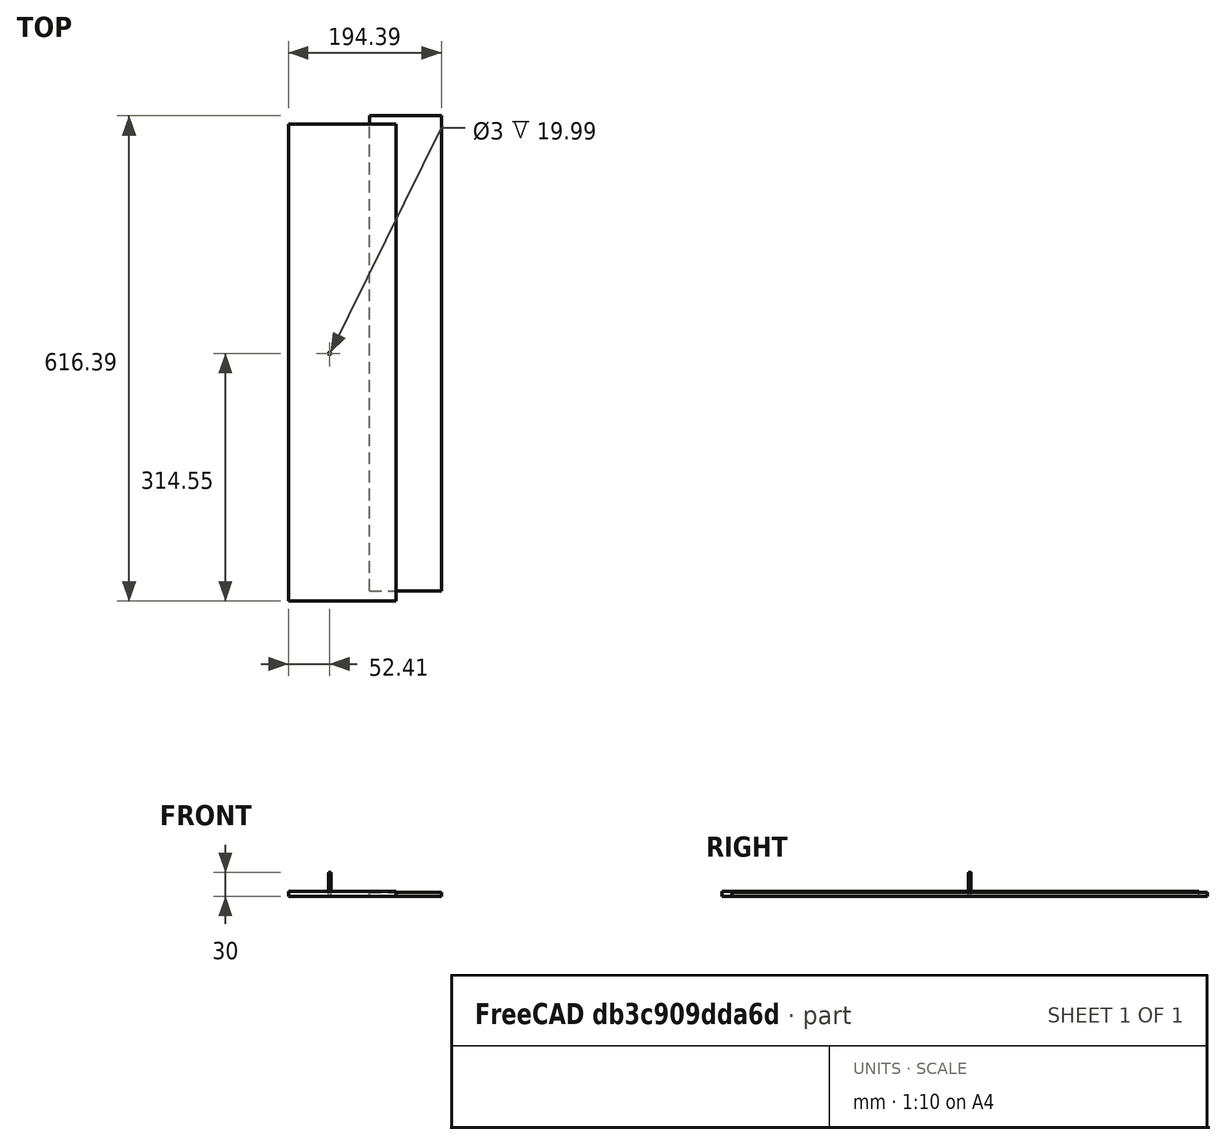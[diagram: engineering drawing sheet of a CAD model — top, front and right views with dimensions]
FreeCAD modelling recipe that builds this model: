
FCSTD DOCUMENT  (FreeCAD 0.22R34651 (Git))
Label: composit_stand7_PP_cut
License: All rights reserved
LicenseURL: http://en.wikipedia.org/wiki/All_rights_reserved
objects: App::DocumentObjectGroup×7, Part::FeaturePython×6, Path::FeaturePython×5, Part::Part2DObjectPython×4, App::FeaturePython×1, App::Link×1, Path::FeatureCompound×1
note: 14 computed .brp shape members not serialized (recipe doc carries the construction recipe); baked Part::Feature solids carry a one-line shape summary decoded from their .brp
EXTERNAL_REF file=composit_stand7.FCStd obj=Body003

FEATURE [App::DocumentObjectGroup] Group003  label="sink2_Group"
FEATURE [App::DocumentObjectGroup] Group001  label="unfolds"
  Group = -> [Group003]
FEATURE [App::FeaturePython] SetupSheet  # Path/CAM operation (typed FeaturePython)
  ClearanceHeightExpression = OpStockZMax+SetupSheet.ClearanceHeightOffset
  ClearanceHeightOffset = 5
  CoolantMode = 0
  CoolantModes = None | Flood | Mist
  FinalDepthExpression = -0.1 mm
  HorizRapid = 0
  ProfileDirection = 1
  ProfileSide = 0
  ProfileUseComp = true
  ProfileprocessCircles = true
  ProfileprocessHoles = true
  ProfileprocessPerimeter = true
  SafeHeightExpression = OpStockZMax+SetupSheet.SafeHeightOffset
  SafeHeightOffset = 3
  StartDepthExpression = 3 mm
  StepDownExpression = 4 mm
  VertRapid = 0
FEATURE [Part::FeaturePython] ToolBit  label="3.175mm Endmill"  # Path/CAM toolbit (typed FeaturePython)
  BitPropertyNames = Chipload | CuttingEdgeHeight | Diameter | Flutes | Length | Material | ShankDiameter | SpindleDirection
  BitShape = <path>
  Chipload = 0
  CuttingEdgeHeight = 30
  Diameter = 3.17
  Flutes = 0
  Length = 10
  Material = 0
  ShankDiameter = 3
  ShapeName = endmill
  SpindleDirection = 0
FEATURE [Path::FeaturePython] __175mm_Endmill  label="3.175mm Endmill001"  # Path/CAM operation (typed FeaturePython)
  HorizFeed = 33.3333
  HorizRapid = 0
  SpindleDir = 0
  SpindleSpeed = 18000
  Tool = -> ToolBit
  ToolNumber = 1
  VertFeed = 35
  VertRapid = 0
  expr: HorizRapid = SetupSheet.HorizRapid
  expr: VertRapid = SetupSheet.VertRapid
FEATURE [App::DocumentObjectGroup] Tools
  Group = -> [__175mm_Endmill]
FEATURE [Part::Part2DObjectPython] Rectangle  # Draft 2D object (typed FeaturePython)
  Area = 0
  ChamferSize = 0
  Columns = 1
  FilletRadius = 0
  Height = 1500
  Length = 1500
  MakeFace = false
  Rows = 1
FEATURE [App::Link] Link  label="top_dropper_fix"
  LinkedObject = -> <external composit_stand7.FCStd>#Body003
FEATURE [App::DocumentObjectGroup] Group  label="parts"
  Group = -> [Link]
FEATURE [Part::FeaturePython] Clone  label="Model-top_dropper_fix"  # Draft clone (typed FeaturePython)
  AttacherType = Attacher::AttachEngine3D
  Fuse = false
  Objects = -> [Link]
  PathResource = Model
  Placement = pos=(38.9812,0,5) rot=(0.707107,0.707107,0;3.14159rad)
  Scale = (1,1,1)
FEATURE [Part::FeaturePython] Clone001  label="Model-top_dropper_fix001"  # Draft clone (typed FeaturePython)
  AttacherType = Attacher::AttachEngine3D
  Fuse = false
  Objects = -> [Link]
  PathResource = Model
  Placement = pos=(82.6289,0,5) rot=(0.707107,0.707107,0;3.14159rad)
  Scale = (1,1,1)
FEATURE [App::DocumentObjectGroup] Model
  Group = -> [Clone,Clone001]
FEATURE [Part::FeaturePython] Stock  # WARN: FeaturePython — macro-defined, semantics opaque (R4)
  Base = -> Model
  ExtXneg = 1
  ExtXpos = 1
  ExtYneg = 1
  ExtYpos = 1
  ExtZneg = 0
  ExtZpos = 1
  Placement = pos=(-51.4071,-313.554,-1.68e-13) rot=(0,0,1;0rad)
  StockType = FromBase
FEATURE [Path::FeaturePython] Profile  # Path/CAM operation (typed FeaturePython)
  Active = false
  AreaParams:
    Tolerance = 1e-07
    FitArcs = True
    Simplify = False
    CleanDistance = 0.0
    Accuracy = 0.01
    Unit = 1.0
    MinArcPoints = 4
    MaxArcPoints = 100
    ClipperScale = 10000000.0
    Fill = 0
    Coplanar = 0
    Reorient = True
    Outline = False
    Explode = False
    OpenMode = 0
    Deflection = 0.01
    SubjectFill = 0
    ClipFill = 0
    Offset = -1.585
    ExtraPass = 0
    Stepover = 0.0
    LastStepover = 0.0
    JoinType = 0
    EndType = 0
    MiterLimit = 2.0
    RoundPrecision = 0.0
    PocketMode = 0
    ToolRadius = 1.0
    PocketExtraOffset = 0.0
    PocketStepover = 0.0
    PocketLastStepover = 0.0
    FromCenter = False
    Angle = 45.0
    AngleShift = 0.0
    Shift = 0.0
    Thicken = False
    SectionCount = -1
    Stepdown = 1.0
    SectionOffset = 0.0
    SectionTolerance = 1e-07
    SectionMode = 2
    Project = False
  Base = -> [Clone,Clone001]
  ClearanceHeight = 11
  CoolantMode = 0
  CycleTime = 00:01:07
  Direction = 1
  FinalDepth = -0.1
  HandleMultipleFeatures = 0
  JoinType = 0
  MiterLimit = 0.1
  OffsetExtra = 0
  OpFinalDepth = -1.68e-13
  OpStartDepth = 6
  OpStockZMax = 6
  OpStockZMin = -1.68e-13
  OpToolDiameter = 3.17
  PathParams = {'orientation': 1, 'feedrate': 33.333333333333336, 'feedrate_v': 35.0, 'verbose': True, 'resume_height': 8.999999999999858, 'retraction': 10.999999999999858, 'return_end': True, 'preamble': False, 'start': Vector (166.08630580869018, 278.409351642555, 10.999999999999858)}
  SafeHeight = 9
  Side = 0
  SplitArcs = false
  StartDepth = 3
  StartPoint = (0,0,0)
  StepDown = 4
  ToolController = -> __175mm_Endmill
  UseComp = true
  UseStartPoint = false
  processCircles = true
  processHoles = true
  processPerimeter = false
  expr: ClearanceHeight = OpStockZMax + SetupSheet.ClearanceHeightOffset
  expr: FinalDepth = -0.1 mm
  expr: SafeHeight = OpStockZMax + SetupSheet.SafeHeightOffset
  expr: StartDepth = 3 mm
  expr: StepDown = 4 mm
FEATURE [Path::FeaturePython] Profile001  # Path/CAM operation (typed FeaturePython)
  Active = true
  AreaParams:
    Tolerance = 1e-07
    FitArcs = True
    Simplify = False
    CleanDistance = 0.0
    Accuracy = 0.01
    Unit = 1.0
    MinArcPoints = 4
    MaxArcPoints = 100
    ClipperScale = 10000000.0
    Fill = 0
    Coplanar = 0
    Reorient = True
    Outline = False
    Explode = False
    OpenMode = 0
    Deflection = 0.01
    SubjectFill = 0
    ClipFill = 0
    Offset = 1.585
    ExtraPass = 0
    Stepover = 0.0
    LastStepover = 0.0
    JoinType = 0
    EndType = 0
    MiterLimit = 2.0
    RoundPrecision = 0.0
    PocketMode = 0
    ToolRadius = 1.0
    PocketExtraOffset = 0.0
    PocketStepover = 0.0
    PocketLastStepover = 0.0
    FromCenter = False
    Angle = 45.0
    AngleShift = 0.0
    Shift = 0.0
    Thicken = False
    SectionCount = -1
    Stepdown = 1.0
    SectionOffset = 0.0
    SectionTolerance = 1e-07
    SectionMode = 2
    Project = False
  Base = -> [Clone,Clone001]
  ClearanceHeight = 11
  CoolantMode = 0
  CycleTime = 00:01:29
  Direction = 1
  FinalDepth = -0.1
  HandleMultipleFeatures = 0
  JoinType = 0
  MiterLimit = 0.1
  OffsetExtra = 0
  OpFinalDepth = -1.68e-13
  OpStartDepth = 6
  OpStockZMax = 6
  OpStockZMin = -1.68e-13
  OpToolDiameter = 3.17
  PathParams = {'orientation': 0, 'feedrate': 33.333333333333336, 'feedrate_v': 35.0, 'verbose': True, 'resume_height': 8.999999999999858, 'retraction': 10.999999999999858, 'return_end': True, 'preamble': False, 'start': Vector (141.29940012354697, 301.18747595227586, 10.999999999999858)}
  SafeHeight = 9
  Side = 0
  SplitArcs = false
  StartDepth = 3
  StartPoint = (0,0,0)
  StepDown = 4
  ToolController = -> __175mm_Endmill
  UseComp = true
  UseStartPoint = false
  processCircles = false
  processHoles = false
  processPerimeter = true
  expr: Base = <<Profile>>.Base
  expr: ClearanceHeight = OpStockZMax + SetupSheet.ClearanceHeightOffset
  expr: FinalDepth = -0.1 mm
  expr: SafeHeight = OpStockZMax + SetupSheet.SafeHeightOffset
  expr: StartDepth = 3 mm
  expr: StepDown = 4 mm
FEATURE [Path::FeaturePython] Pocket_Shape  # Path/CAM operation (typed FeaturePython)
  Active = true
  AreaParams:
    Tolerance = 1e-07
    FitArcs = True
    Simplify = False
    CleanDistance = 0.0
    Accuracy = 0.01
    Unit = 1.0
    MinArcPoints = 4
    MaxArcPoints = 100
    ClipperScale = 10000000.0
    Fill = 0
    Coplanar = 0
    Reorient = True
    Outline = False
    Explode = False
    OpenMode = 0
    Deflection = 0.01
    SubjectFill = 0
    ClipFill = 0
    Offset = 0.0
    ExtraPass = 0
    Stepover = 0.0
    LastStepover = 0.0
    JoinType = 0
    EndType = 0
    MiterLimit = 2.0
    RoundPrecision = 0.0
    PocketMode = 2
    ToolRadius = 1.585
    PocketExtraOffset = 0.0
    PocketStepover = 2.219
    PocketLastStepover = 0.0
    FromCenter = True
    Angle = 45.0
    AngleShift = 0.0
    Shift = 0.0
    Thicken = False
    SectionCount = -1
    Stepdown = 1.0
    SectionOffset = 0.0
    SectionTolerance = 1e-07
    SectionMode = 2
    Project = False
  Base = -> [Clone,Clone001]
  ClearanceHeight = 11
  CoolantMode = 0
  CutMode = 0
  CycleTime = 00:02:52
  ExtensionCorners = true
  ExtensionLengthDefault = 1.585
  ExtraOffset = 0
  FinalDepth = 2.5
  FinishDepth = 0
  KeepToolDown = false
  MinTravel = false
  OffsetPattern = 1
  OpFinalDepth = 2.5
  OpStartDepth = 6
  OpStockZMax = 6
  OpStockZMin = -1.68e-13
  OpToolDiameter = 3.17
  PathParams = {'orientation': 1, 'feedrate': 33.333333333333336, 'feedrate_v': 35.0, 'verbose': True, 'resume_height': 8.999999999999858, 'retraction': 10.999999999999858, 'return_end': True, 'preamble': False, 'start': Vector (129.9501486831128, 252.23587670492103, 10.999999999999858)}
  PocketLastStepOver = 0
  SafeHeight = 9
  SplitArcs = false
  StartAt = 0
  StartDepth = 3
  StartPoint = (0,0,0)
  StepDown = 4
  StepOver = 70
  ToolController = -> __175mm_Endmill
  UseOutline = true
  UseRestMachining = false
  UseStartPoint = false
  ZigZagAngle = 45
  expr: ClearanceHeight = OpStockZMax + SetupSheet.ClearanceHeightOffset
  expr: ExtensionLengthDefault = OpToolDiameter / 2
  expr: SafeHeight = OpStockZMax + SetupSheet.SafeHeightOffset
  expr: StartDepth = 3 mm
  expr: StepDown = 4 mm
FEATURE [App::DocumentObjectGroup] Operations
  Group = -> [Profile,Pocket_Shape,Profile001]
FEATURE [Path::FeaturePython] Job  # Path/CAM operation (typed FeaturePython)
  CycleTime = 00:04:21
  Fixtures = G54
  GeometryTolerance = 0.01
  JobType = 0
  LastPostProcessDate = 2023-10-19 12:10:22.027677
  LastPostProcessOutput = <userpath>/2CAF-B51C/Job.tap
  Model = -> Model
  Operations = -> Operations
  OrderOutputBy = 2
  PostProcessor = 3
  PostProcessorOutputFile = %j.tap
  SetupSheet = -> SetupSheet
  SplitOutput = false
  Stock = -> Stock
  Tools = -> Tools
FEATURE [App::DocumentObjectGroup] Group002  label="jobs"
  Group = -> [Job]
FEATURE [Part::Part2DObjectPython] Line  # Draft 2D object (typed FeaturePython)
  Area = 0
  ChamferSize = 0
  Closed = false
  End = (75.212,-201.344,1.62e-14)
  FilletRadius = 0
  Length = 3.2
  MakeFace = true
  Placement = pos=(77.9833,-199.744,1.66e-14) rot=(0,0,1;0rad)
  Points = (2) [(0,0,0),(-2.77128,-1.6,-3.6752e-16)]
  Start = (77.9833,-199.744,1.66e-14)
  Subdivisions = 0
FEATURE [Part::Part2DObjectPython] Line001  # Draft 2D object (typed FeaturePython)
  Area = 0
  ChamferSize = 0
  Closed = false
  End = (194.18,-199.744,1.66e-14)
  FilletRadius = 0
  Length = 116.196
  MakeFace = true
  Placement = pos=(77.9833,-199.744,1.66e-14) rot=(0,0,1;0rad)
  Points = (2) [(0,0,0),(116.196,0,0)]
  Start = (77.9833,-199.744,1.66e-14)
  Subdivisions = 0
FEATURE [Path::FeatureCompound] compound
  ClearanceHeight = 0
  SafeHeight = 0
  UsePlacements = false
FEATURE [Part::FeaturePython] BoundBox  label="BoundBox of Model-top_dropper_fix"  # WARN: FeaturePython — macro-defined, semantics opaque (R4)
  Center = (96.4812,0,2.5)
  CompoundTraversal = 0
  OrientMode = 0
  Padding = 0
  Precision = false
  ScaleFactor = 1
  ShapeLink = -> Clone
  Size = (91,603.685,5)
FEATURE [Part::FeaturePython] Point  # WARN: FeaturePython — macro-defined, semantics opaque (R4)
  Placement = pos=(82,215,0) rot=(0,0,1;0rad)
  X = 82
  Y = 215
  Z = 0
FEATURE [Part::Part2DObjectPython] Line002  # Draft 2D object (typed FeaturePython)
  Area = 0
  ChamferSize = 0
  Closed = false
  End = (0,215,0)
  FilletRadius = 0
  Length = 82
  MakeFace = true
  Placement = pos=(82,215,0) rot=(0,1,0;3.14159rad)
  Points = (2) [(0,0,0),(82,0,0)]
  Start = (82,215,0)
  Subdivisions = 0
note: 1 file-system path scrubbed to <path> (originals preserved in the JSON sidecar)
